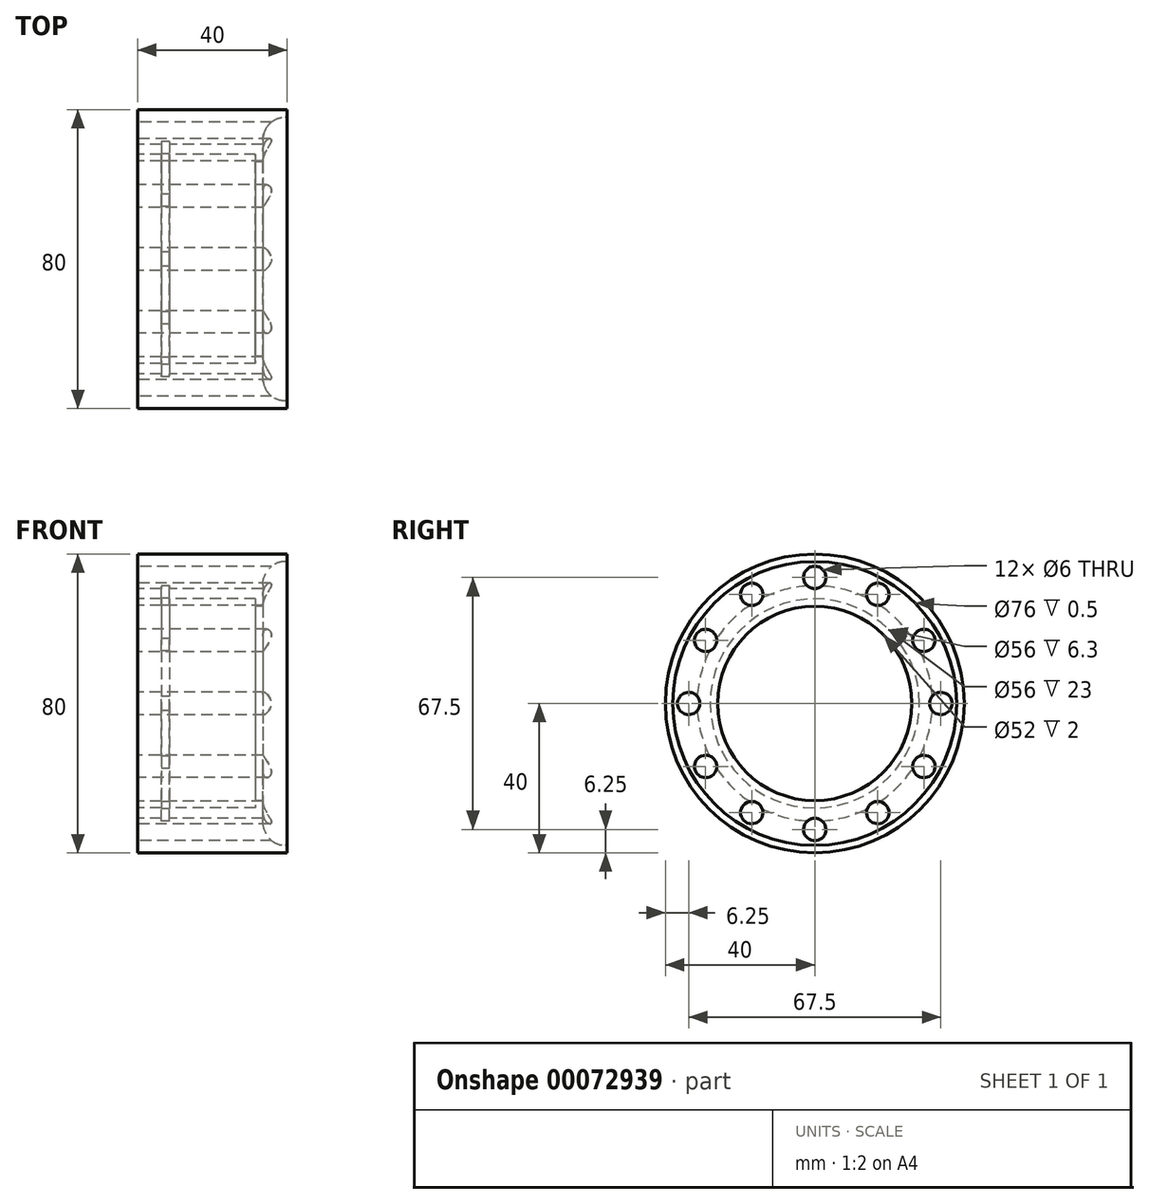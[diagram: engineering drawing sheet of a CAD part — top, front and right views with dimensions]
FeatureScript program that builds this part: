
annotation { "Feature Type Name" : "Feature", "Feature Type Description" : "" }
export const myFeature = defineFeature(function(context is Context, id is Id, definition is map)
    precondition{}
    {
        {
            var Q0;
            Q0=qCreatedBy(makeId("Top.planeOp"),FACE);
            var sketch = newSketch(context, id + "F0", { "sketchPlane" : qUnion([Q0])});
            skLineSegment(sketch, "E0", {"start": v(-20, 40) * mm, "end": v(20, 40) * mm});
            skLineSegment(sketch, "E1", {"start": v(20, 40) * mm, "end": v(20, 38) * mm});
            skLineSegment(sketch, "E2", {"start": v(20, 38) * mm, "end": v(19.5, 38) * mm});
            skLineSegment(sketch, "E3", {"start": v(13.5, 32) * mm, "end": v(13.5, 26) * mm});
            skLineSegment(sketch, "E4", {"start": v(13.5, 26) * mm, "end": v(11.5, 26) * mm});
            skLineSegment(sketch, "E5", {"start": v(11.5, 26) * mm, "end": v(11.5, 28) * mm});
            skLineSegment(sketch, "E6", {"start": v(11.5, 28) * mm, "end": v(-11.5, 28) * mm});
            skLineSegment(sketch, "E7", {"start": v(-20, 28) * mm, "end": v(-20, 40) * mm});
            skPoint(sketch, "E8.visualSharp", {"position": v(13.5, 38) * mm});
            skArc(sketch, "E8.filletArc", {"start": v(19.5, 38) * mm, "mid": v(15.26, 36.24) * mm, "end": v(13.5, 32) * mm});
            skLineSegment(sketch, "E9", {"start": v(-13.7, 28) * mm, "end": v(-13.7, 31.5) * mm});
            skLineSegment(sketch, "E10", {"start": v(-13.7, 31.5) * mm, "end": v(-11.5, 31.5) * mm});
            skLineSegment(sketch, "E11", {"start": v(-11.5, 31.5) * mm, "end": v(-11.5, 28) * mm});
            skLineSegment(sketch, "E12.trimOffspring", {"start": v(-13.7, 28) * mm, "end": v(-20, 28) * mm});
            skLineSegment(sketch, "E13", {"start": v(-90, 0) * mm, "end": v(112.5, 0) * mm, "construction": true});
            skSolve(sketch);
        }
        {
            var Q0;
            Q0=makeQuery(id+"F0.imprint","IMPRINT",FACE,{"disambiguationData":[TD([[makeQuery(id+"F0.imprint","IMPRINT",EDGE,{"derivedFrom":sQuery(id+"F0.wireOp",EDGE,"E0")}),-1.0]])]});
            var Q1;
            Q1=sQuery(id+"F0.wireOp",EDGE,"E13");
            revolve(context, id + "F1", {"entities" : qUnion([Q0]), "axis" : qUnion([Q1]), "revolveType" : RevolveType.FULL});
        }
        {
            var Q0;
            Q0=makeQuery(id+"F1.opRevolve","SWEPT_FACE",FACE,{"disambiguationData":[OSD([sQuery(id+"F0.wireOp",EDGE,"E7")])]});
            var sketch = newSketch(context, id + "F2", { "sketchPlane" : qUnion([Q0])});
            skCircle(sketch, "E14", {"center": v(0, 33.75) * mm, "radius": 3 * mm});
            skCircle(sketch, "E15.1.0", {"center": v(-16.88, 29.23) * mm, "radius": 3 * mm});
            skCircle(sketch, "E15.2.0", {"center": v(-29.23, 16.88) * mm, "radius": 3 * mm});
            skPoint(sketch, "E15.center", {"position": v(0, 0) * mm});
            skCircle(sketch, "E16.1.3.0", {"center": v(-33.75, 0) * mm, "radius": 3 * mm});
            skCircle(sketch, "E16.1.4.0", {"center": v(-29.23, -16.88) * mm, "radius": 3 * mm});
            skCircle(sketch, "E16.1.5.0", {"center": v(-16.88, -29.23) * mm, "radius": 3 * mm});
            skCircle(sketch, "E16.1.6.0", {"center": v(0, -33.75) * mm, "radius": 3 * mm});
            skCircle(sketch, "E16.1.7.0", {"center": v(16.88, -29.23) * mm, "radius": 3 * mm});
            skCircle(sketch, "E16.1.8.0", {"center": v(29.23, -16.88) * mm, "radius": 3 * mm});
            skCircle(sketch, "E16.1.9.0", {"center": v(33.75, 0) * mm, "radius": 3 * mm});
            skCircle(sketch, "E16.1.10.0", {"center": v(29.23, 16.88) * mm, "radius": 3 * mm});
            skCircle(sketch, "E16.1.11.0", {"center": v(16.88, 29.23) * mm, "radius": 3 * mm});
            skSolve(sketch);
        }
        {
            var Q0;
            Q0=qSketchRegion(id+"F2",true);
            extrude(context, id + "F3", {"entities" : qUnion([Q0]), "operationType" : NewBodyOperationType.REMOVE, "endBound" : BoundingType.THROUGH_ALL, "oppositeDirection" : true, "depth" : 25 * mm});
        }
    });
